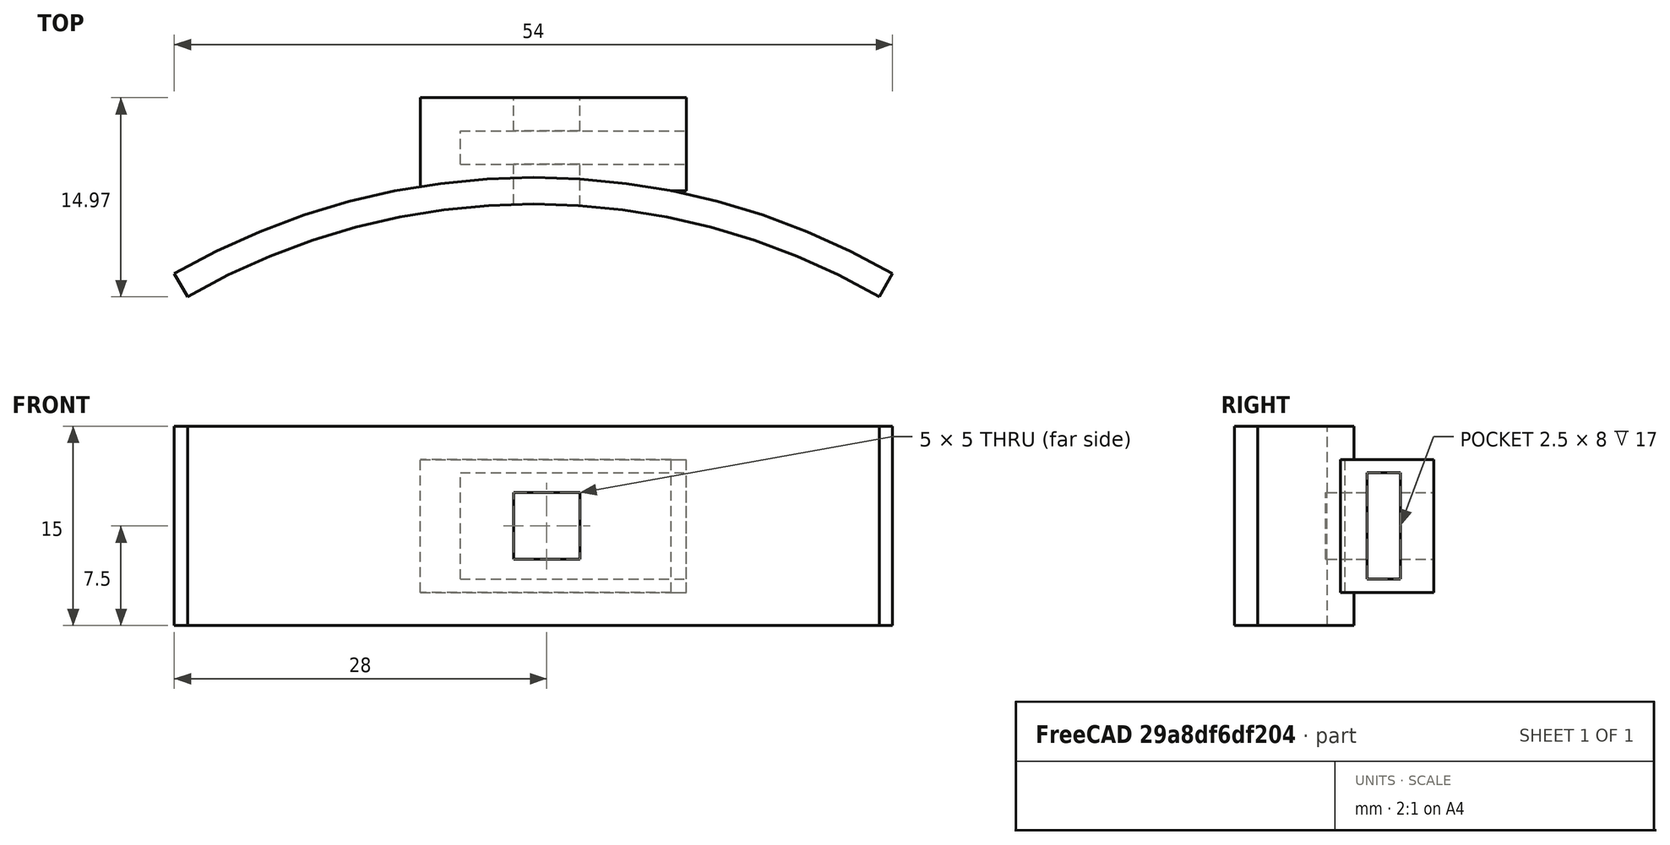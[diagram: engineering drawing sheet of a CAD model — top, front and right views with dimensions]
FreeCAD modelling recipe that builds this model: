
FCSTD DOCUMENT  (FreeCAD 0.16R4924 (Git))
Label: outer_latch
License: All rights reserved
LicenseURL: http://en.wikipedia.org/wiki/All_rights_reserved
objects: Part::Cut×3, Part::Box×3, Part::Cylinder×2, Part::MultiFuse×2
note: 10 computed .brp shape members not serialized (recipe doc carries the construction recipe); baked Part::Feature solids carry a one-line shape summary decoded from their .brp

FEATURE [Part::Cylinder] Cylinder  label="bottle_wall"
  Angle = 60
  Height = 15
  Placement = pos=(8.5,-7,0) rot=(0,0,1;1.0472rad)
  Radius = 54
FEATURE [Part::Cylinder] Cylinder001  label="bottle_wall001"
  Angle = 60
  Height = 15
  Placement = pos=(8.5,-7,0) rot=(0,0,1;1.0472rad)
  Radius = 52
FEATURE [Part::Cut] Cut
  Base = -> Cylinder
  Placement = pos=(0,-2,0) rot=(0,0,1;0rad)
  Tool = -> Cylinder001
FEATURE [Part::Box] Box  label="pin_opening"
  Height = 5
  Length = 5
  Placement = pos=(7,42,5) rot=(0,0,1;0rad)
  Width = 20
FEATURE [Part::Box] Box001  label="latch"
  Height = 10
  Length = 20
  Placement = pos=(0,44,2.5) rot=(0,0,1;0rad)
  Width = 7
FEATURE [Part::MultiFuse] Fusion
  Shapes = -> [Cut,Box001]
FEATURE [Part::MultiFuse] Fusion001
  Shapes = -> [Fusion,Box001]
FEATURE [Part::Cut] Cut001
  Base = -> Fusion001
  Tool = -> Box
FEATURE [Part::Box] Box002  label="slot"
  Height = 8
  Length = 20
  Placement = pos=(3,46,3.5) rot=(0,0,1;0rad)
  Width = 2.5
FEATURE [Part::Cut] Cut002
  Base = -> Cut001
  Tool = -> Box002
